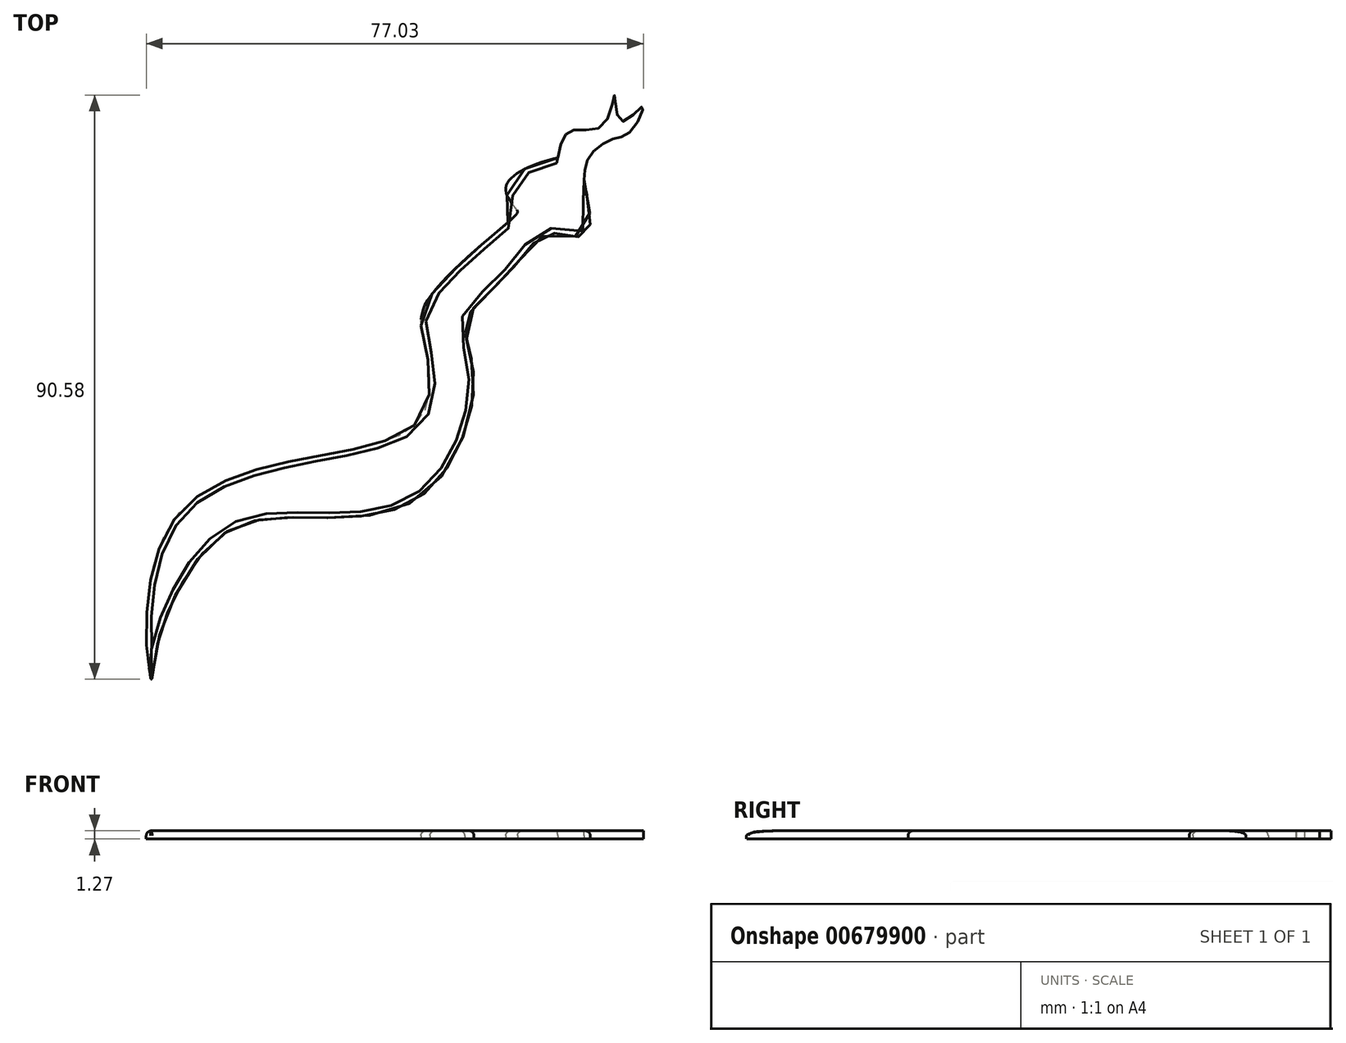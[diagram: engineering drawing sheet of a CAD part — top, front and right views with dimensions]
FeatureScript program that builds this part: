
annotation { "Feature Type Name" : "Feature", "Feature Type Description" : "" }
export const myFeature = defineFeature(function(context is Context, id is Id, definition is map)
    precondition{}
    {
        {
            var Q0;
            Q0=qCreatedBy(makeId("Top.planeOp"),FACE);
            var sketch = newSketch(context, id + "F0", { "sketchPlane" : qUnion([Q0])});
            skFitSpline(sketch, "E0", {"points": [v(-35.2, -34.17) * mm, v(-31, -8.64) * mm, v(5.2, 4.82) * mm, v(7.3, 17.24) * mm, v(7.82, 24.76) * mm, v(21.28, 37.7) * mm, v(21.46, 38.58) * mm, v(19.88, 42.42) * mm, v(29.85, 46.8) * mm, v(31.6, 44.52) * mm, v(32.3, 34.73) * mm, v(26.7, 34.9) * mm, v(20.23, 28.78) * mm, v(13.59, 21.26) * mm, v(14.81, 13.22) * mm, v(7.12, -5.5) * mm, v(-11.77, -9.17) * mm, v(-24.36, -11.96) * mm, v(-34.16, -28.58) * mm, v(-35.2, -34.17) * mm]});
            skFitSpline(sketch, "E1", {"points": [v(27.82, 46.6) * mm, v(29.85, 50.84) * mm, v(34.91, 51.7) * mm, v(36.65, 56.34) * mm, v(37.66, 52.29) * mm, v(41, 54.6) * mm, v(39.26, 50.84) * mm, v(36.36, 49.53) * mm, v(32.74, 46.8) * mm, v(31.92, 43.17) * mm], "startDerivative": vector(9.43, 48.14) * mm, "endDerivative": vector(-1.6, -36.26) * mm});
            skSolve(sketch);
        }
        {
            var Q0;
            Q0 = qSketchRegion(id + "F0", true);
            extrude(context, id + "F1", {"entities" : qUnion([Q0]), "depth" : 1.27 * mm, "offsetDistance" : 25.4 * mm});
        }
        {
            var Q0;
            Q0=makeQuery(id+"F1.opExtrude","CAP_EDGE",EDGE,{"disambiguationData":[OSD([sQuery(id+"F0.wireOp",EDGE,"E0")])],"isStart":false});
            fillet(context, id + "F2", {"entities" : qUnion([Q0]), "radius" : 0.76 * mm, "tangentPropagation" : true, "allowEdgeOverflow" : false});
        }
    });
